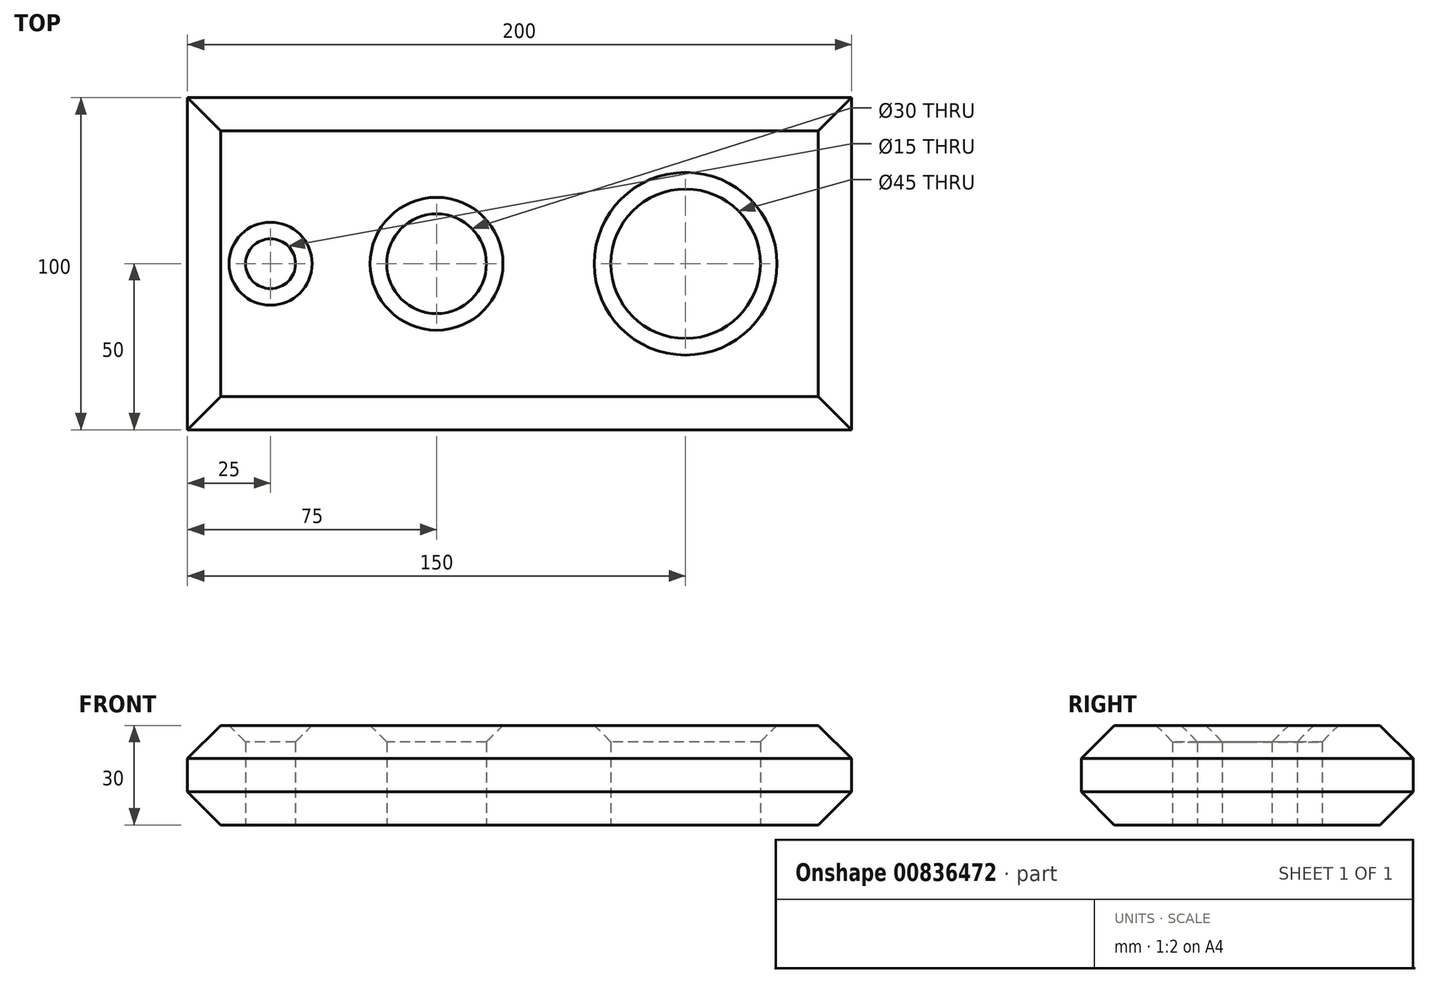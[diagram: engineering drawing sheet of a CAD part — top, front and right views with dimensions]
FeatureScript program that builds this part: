
annotation { "Feature Type Name" : "Feature", "Feature Type Description" : "" }
export const myFeature = defineFeature(function(context is Context, id is Id, definition is map)
    precondition{}
    {
        {
            var Q0;
            Q0=qCreatedBy(makeId("Top.planeOp"),FACE);
            var sketch = newSketch(context, id + "F0", { "sketchPlane" : qUnion([Q0])});
            skLineSegment(sketch, "E0.bottom", {"start": v(0, 0) * mm, "end": v(200, 0) * mm});
            skLineSegment(sketch, "E0.top", {"start": v(0, 100) * mm, "end": v(200, 100) * mm});
            skLineSegment(sketch, "E0.left", {"start": v(0, 0) * mm, "end": v(0, 100) * mm});
            skLineSegment(sketch, "E0.right", {"start": v(200, 0) * mm, "end": v(200, 100) * mm});
            skCircle(sketch, "E1", {"center": v(25, 50) * mm, "radius": 7.5 * mm});
            skCircle(sketch, "E2", {"center": v(75, 50) * mm, "radius": 15 * mm});
            skCircle(sketch, "E3", {"center": v(150, 50) * mm, "radius": 22.5 * mm});
            skSolve(sketch);
        }
        {
            var Q0;
            Q0 = qSketchRegion(id + "F0", true);
            extrude(context, id + "F1", {"entities" : qUnion([Q0]), "depth" : 30 * mm, "offsetDistance" : 25 * mm});
        }
        {
            var Q0;
            Q0=makeQuery(id+"F1.opExtrude","CAP_EDGE",EDGE,{"disambiguationData":[OSD([sQuery(id+"F0.wireOp",EDGE,"E0.bottom")])],"isStart":false});
            var Q1;
            Q1=makeQuery(id+"F1.opExtrude","CAP_EDGE",EDGE,{"disambiguationData":[OSD([sQuery(id+"F0.wireOp",EDGE,"E0.right")])],"isStart":false});
            var Q2;
            Q2=makeQuery(id+"F1.opExtrude","CAP_EDGE",EDGE,{"disambiguationData":[OSD([sQuery(id+"F0.wireOp",EDGE,"E0.top")])],"isStart":false});
            var Q3;
            Q3=makeQuery(id+"F1.opExtrude","CAP_EDGE",EDGE,{"disambiguationData":[OSD([sQuery(id+"F0.wireOp",EDGE,"E0.left")])],"isStart":false});
            chamfer(context, id + "F2", {"entities" : qUnion([Q0, Q1, Q2, Q3]), "chamferType" : ChamferType.OFFSET_ANGLE, "width" : 10 * mm, "oppositeDirection" : false, "angle" : 45 * degree, "tangentPropagation" : true});
        }
        {
            var Q0;
            Q0=makeQuery(id+"F1.opExtrude","CAP_EDGE",EDGE,{"disambiguationData":[OSD([sQuery(id+"F0.wireOp",EDGE,"E1")])],"isStart":false});
            var Q1;
            Q1=makeQuery(id+"F1.opExtrude","CAP_EDGE",EDGE,{"disambiguationData":[OSD([sQuery(id+"F0.wireOp",EDGE,"E2")])],"isStart":false});
            var Q2;
            Q2=makeQuery(id+"F1.opExtrude","CAP_EDGE",EDGE,{"disambiguationData":[OSD([sQuery(id+"F0.wireOp",EDGE,"E3")])],"isStart":false});
            chamfer(context, id + "F3", {"entities" : qUnion([Q0, Q1, Q2]), "chamferType" : ChamferType.OFFSET_ANGLE, "width" : 5 * mm, "oppositeDirection" : false, "angle" : 45 * degree, "tangentPropagation" : true});
        }
        {
            var Q0;
            Q0=makeQuery(id+"F1.opExtrude","CAP_EDGE",EDGE,{"disambiguationData":[OSD([sQuery(id+"F0.wireOp",EDGE,"E0.left")])],"isStart":true});
            var Q1;
            Q1=makeQuery(id+"F1.opExtrude","CAP_EDGE",EDGE,{"disambiguationData":[OSD([sQuery(id+"F0.wireOp",EDGE,"E0.bottom")])],"isStart":true});
            var Q2;
            Q2=makeQuery(id+"F1.opExtrude","CAP_EDGE",EDGE,{"disambiguationData":[OSD([sQuery(id+"F0.wireOp",EDGE,"E0.top")])],"isStart":true});
            var Q3;
            Q3=makeQuery(id+"F1.opExtrude","CAP_EDGE",EDGE,{"disambiguationData":[OSD([sQuery(id+"F0.wireOp",EDGE,"E0.right")])],"isStart":true});
            chamfer(context, id + "F4", {"entities" : qUnion([Q0, Q1, Q2, Q3]), "chamferType" : ChamferType.OFFSET_ANGLE, "width" : 10 * mm, "oppositeDirection" : false, "angle" : 45 * degree, "tangentPropagation" : true});
        }
    });
